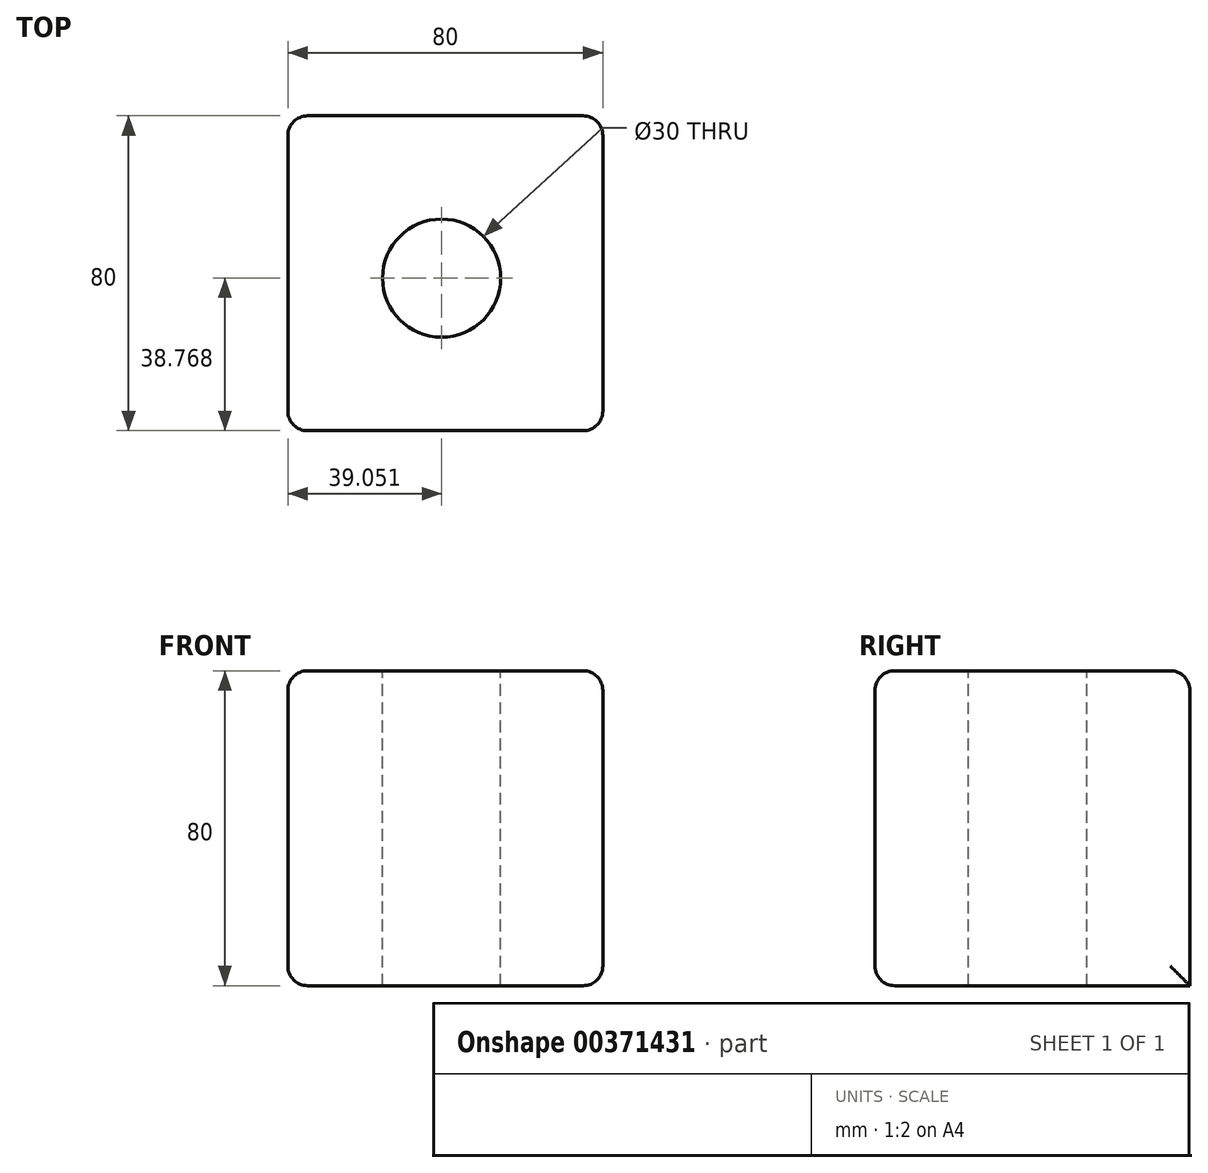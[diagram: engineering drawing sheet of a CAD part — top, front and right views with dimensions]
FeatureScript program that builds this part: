
annotation { "Feature Type Name" : "Feature", "Feature Type Description" : "" }
export const myFeature = defineFeature(function(context is Context, id is Id, definition is map)
    precondition{}
    {
        {
            var Q0;
            Q0=qCreatedBy(makeId("Top.planeOp"),FACE);
            var sketch = newSketch(context, id + "F0", { "sketchPlane" : qUnion([Q0])});
            skLineSegment(sketch, "E0.bottom", {"start": v(-82.66, 80) * mm, "end": v(-2.66, 80) * mm});
            skLineSegment(sketch, "E0.top", {"start": v(-82.66, 0) * mm, "end": v(-2.66, 0) * mm});
            skLineSegment(sketch, "E0.left", {"start": v(-82.66, 80) * mm, "end": v(-82.66, 0) * mm});
            skLineSegment(sketch, "E0.right", {"start": v(-2.66, 80) * mm, "end": v(-2.66, 0) * mm});
            skSolve(sketch);
        }
        {
            var Q0;
            Q0=makeQuery(id+"F0.imprint","IMPRINT",FACE,{"disambiguationData":[TD([[makeQuery(id+"F0.imprint","IMPRINT",EDGE,{"derivedFrom":sQuery(id+"F0.wireOp",EDGE,"E0.bottom")}),-1.0]])]});
            extrude(context, id + "F1", {"entities" : qUnion([Q0]), "depth" : 80 * mm});
        }
        {
            var Q0;
            Q0=makeQuery(id+"F1.opExtrude","CAP_FACE",FACE,{"disambiguationData":[OSD([sQuery(id+"F0.wireOp",EDGE,"E0.bottom"),sQuery(id+"F0.wireOp",EDGE,"E0.top"),sQuery(id+"F0.wireOp",EDGE,"E0.left"),sQuery(id+"F0.wireOp",EDGE,"E0.right")])],"isStart":false});
            var sketch = newSketch(context, id + "F2", { "sketchPlane" : qUnion([Q0])});
            skCircle(sketch, "E1", {"center": v(-43.6, 38.77) * mm, "radius": 15 * mm});
            skSolve(sketch);
        }
        {
            var Q0;
            Q0 = qSketchRegion(id + "F2", true);
            extrude(context, id + "F3", {"entities" : qUnion([Q0]), "operationType" : NewBodyOperationType.ADD, "depth" : 25 * mm});
        }
        {
            var Q0;
            Q0=makeQuery(id+"F3.opExtrude","CAP_FACE",FACE,{"disambiguationData":[OSD([sQuery(id+"F2.wireOp",EDGE,"E1")])],"isStart":false});
            extrude(context, id + "F4", {"entities" : qUnion([Q0]), "operationType" : NewBodyOperationType.REMOVE, "endBound" : BoundingType.THROUGH_ALL, "oppositeDirection" : true, "depth" : 25 * mm});
        }
        {
            var Q0;
            Q0=makeQuery(id+"F1.opExtrude","CAP_EDGE",EDGE,{"disambiguationData":[OSD([sQuery(id+"F0.wireOp",EDGE,"E0.top")])],"isStart":false});
            var Q1;
            Q1=makeQuery(id+"F1.opExtrude","CAP_EDGE",EDGE,{"disambiguationData":[OSD([sQuery(id+"F0.wireOp",EDGE,"E0.left")])],"isStart":false});
            var Q2;
            Q2=makeQuery(id+"F1.opExtrude","CAP_EDGE",EDGE,{"disambiguationData":[OSD([sQuery(id+"F0.wireOp",EDGE,"E0.bottom")])],"isStart":false});
            var Q3;
            Q3=makeQuery(id+"F1.opExtrude","CAP_EDGE",EDGE,{"disambiguationData":[OSD([sQuery(id+"F0.wireOp",EDGE,"E0.right")])],"isStart":false});
            var Q4;
            Q4=makeQuery(id+"F1.opExtrude","SWEPT_EDGE",EDGE,{"disambiguationData":[OSD([sQuery(id+"F0.wireOp",EDGE,"E0.top"),sQuery(id+"F0.wireOp",EDGE,"E0.right")])]});
            var Q5;
            Q5=makeQuery(id+"F1.opExtrude","CAP_EDGE",EDGE,{"disambiguationData":[OSD([sQuery(id+"F0.wireOp",EDGE,"E0.right")])],"isStart":true});
            var Q6;
            Q6=makeQuery(id+"F1.opExtrude","SWEPT_EDGE",EDGE,{"disambiguationData":[OSD([sQuery(id+"F0.wireOp",EDGE,"E0.bottom"),sQuery(id+"F0.wireOp",EDGE,"E0.right")])]});
            var Q7;
            Q7=makeQuery(id+"F1.opExtrude","CAP_EDGE",EDGE,{"disambiguationData":[OSD([sQuery(id+"F0.wireOp",EDGE,"E0.left")])],"isStart":true});
            var Q8;
            Q8=makeQuery(id+"F1.opExtrude","SWEPT_EDGE",EDGE,{"disambiguationData":[OSD([sQuery(id+"F0.wireOp",EDGE,"E0.bottom"),sQuery(id+"F0.wireOp",EDGE,"E0.left")])]});
            var Q9;
            Q9=makeQuery(id+"F1.opExtrude","SWEPT_EDGE",EDGE,{"disambiguationData":[OSD([sQuery(id+"F0.wireOp",EDGE,"E0.top"),sQuery(id+"F0.wireOp",EDGE,"E0.left")])]});
            var Q10;
            Q10=makeQuery(id+"F1.opExtrude","CAP_EDGE",EDGE,{"disambiguationData":[OSD([sQuery(id+"F0.wireOp",EDGE,"E0.top")])],"isStart":true});
            fillet(context, id + "F5", {"entities" : qUnion([Q0, Q1, Q2, Q3, Q4, Q5, Q6, Q7, Q8, Q9, Q10]), "radius" : 5 * mm, "tangentPropagation" : true, "allowEdgeOverflow" : false});
        }
    });
